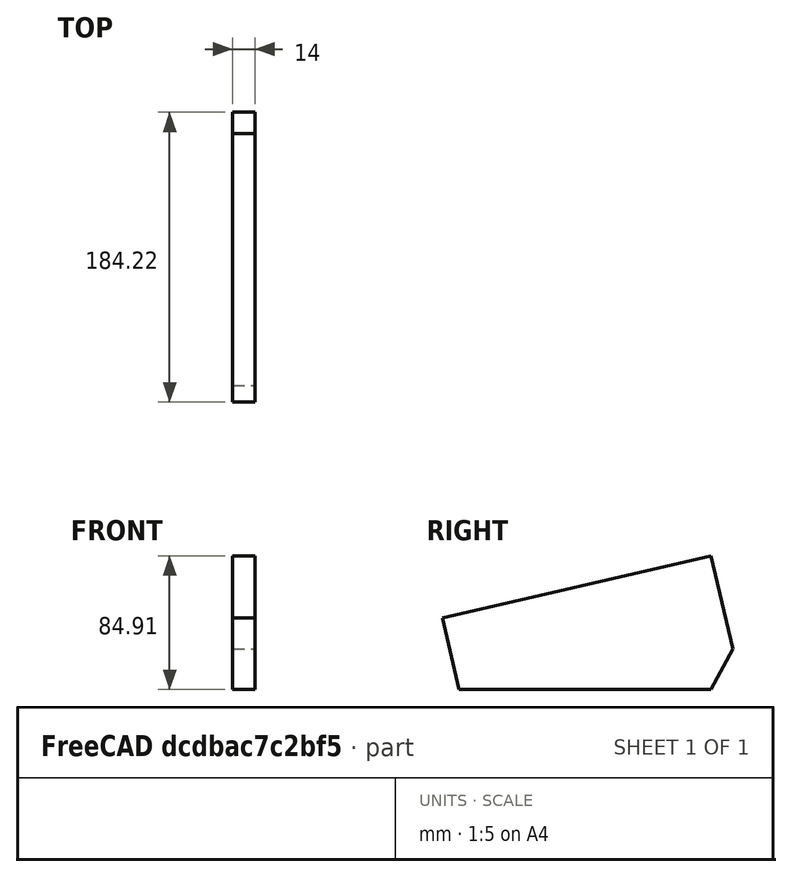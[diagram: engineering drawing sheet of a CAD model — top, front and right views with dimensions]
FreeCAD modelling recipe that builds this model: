
FCSTD DOCUMENT  (FreeCAD 1.0R39109 (Git))
Label: Griffschale
License: All rights reserved
objects: Sketcher::SketchObject×1, PartDesign::Pad×1, PartDesign::Body×1
note: 6 computed .brp shape members not serialized (recipe doc carries the construction recipe); baked Part::Feature solids carry a one-line shape summary decoded from their .brp

FEATURE [Sketcher::SketchObject] Sketch
  ArcFitTolerance = 1e-06
  AttachmentSupport = -> [YZ_Plane]
  FullyConstrained = false
  MakeInternals = false
  MapMode = 5
  Placement = pos=(0,0,0) rot=(0.57735,0.57735,0.57735;2.0944rad)
  sketch-geometry (9):
    g0: LineSegment StartX=-3.97348 StartY=-71.0601 StartZ=0 EndX=156.027 EndY=-71.0601 EndZ=0
    g1: LineSegment StartX=156.027 StartY=-71.0601 StartZ=0 EndX=169.729 EndY=-45.5015 EndZ=0
    g2: LineSegment StartX=169.729 StartY=-45.5015 StartZ=0 EndX=156.027 EndY=13.8508 EndZ=0
    g3: LineSegment StartX=156.027 StartY=13.8508 StartZ=0 EndX=-14.4882 EndY=-25.5156 EndZ=0
    g4: LineSegment StartX=-14.4882 StartY=-25.5156 StartZ=0 EndX=-3.97348 EndY=-71.0601 EndZ=0
    g5: LineSegment [constr] StartX=156.027 StartY=13.8508 StartZ=0 EndX=-211.763 EndY=-71.0601 EndZ=0
    g6: LineSegment [constr] StartX=156.027 StartY=-71.0601 StartZ=0 EndX=-211.763 EndY=-71.0601 EndZ=0
    g7: LineSegment [constr] StartX=156.027 StartY=13.8508 StartZ=0 EndX=156.027 EndY=-71.0601 EndZ=0
    g8: LineSegment [constr] StartX=-14.4882 StartY=-25.5156 StartZ=0 EndX=-14.4882 EndY=-71.0601 EndZ=0
  constraints (23):
    c: Coincident(g0,g1)
    c: Coincident(g1,g2)
    c: Coincident(g2,g3)
    c: Coincident(g3,g4)
    c: Coincident(g4,g0)
    c: Coincident(g5,g2)
    c: Coincident(g6,g0)
    c: Horizontal(g6)
    c: Coincident(g5,g6)
    c: Angle(g6,g5) = 0.226893
    c: Distance(g3) = 175
    c: DistanceX(g0,g0) = 160
    c: Coincident(g7,g2)
    c: Coincident(g7,g0)
    c: Vertical(g7)
    c: Angle(g3,g2) = 1.5708
    c: Angle(g4,g3) = 1.5708
    c: PointOnObject(g3,g5)
    c: PointOnObject(g0,g6)
    c: Coincident(g8,g3)
    c: PointOnObject(g8,g6)
    c: Vertical(g8)
    c: Distance(g1) = 29
FEATURE [PartDesign::Pad] Pad
  Direction = (1,0,0)
  Length = 14
  Length2 = 10
  Placement = pos=(0,0,0) rot=(1,1,1;2.0944rad)
  Profile = -> Sketch
  ReferenceAxis = -> Sketch [N_Axis]
  Refine = true
  Suppressed = false
  Type = 0
FEATURE [PartDesign::Body] Body  label="Körper"
  AllowCompound = false
  Group = -> [Sketch,Pad]
  Origin = -> Origin
  Tip = -> Pad
